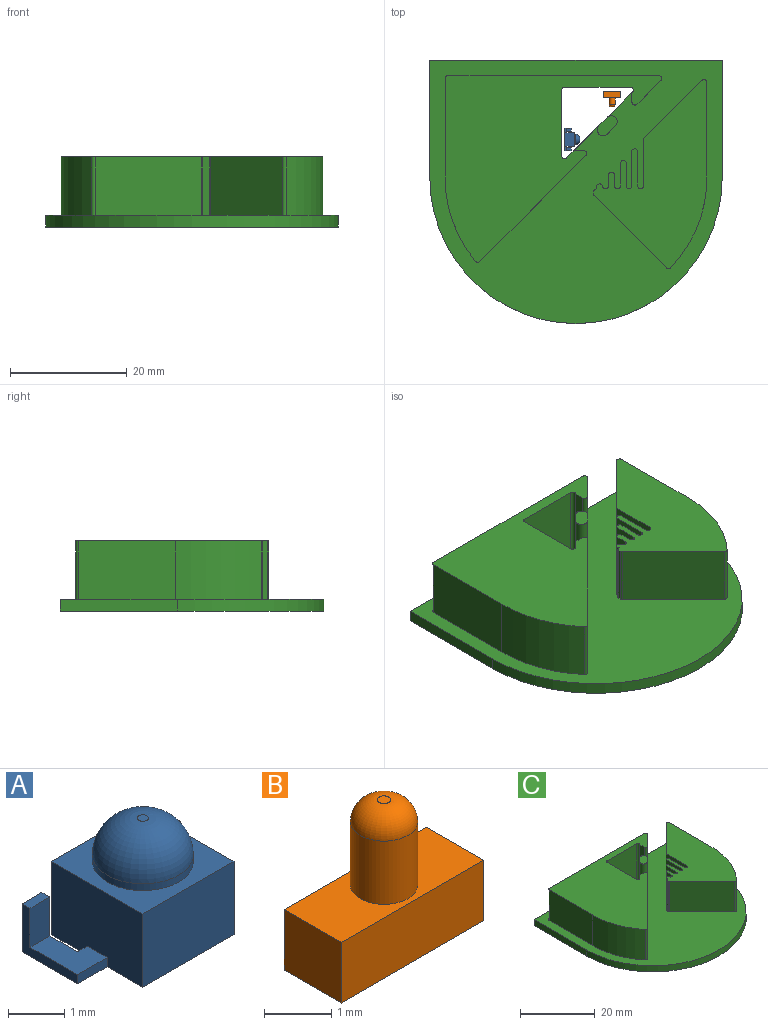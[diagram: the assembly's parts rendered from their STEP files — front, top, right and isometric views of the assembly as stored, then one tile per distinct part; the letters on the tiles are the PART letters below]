
ASSEMBLY  parts=3 mates=2
PART A: 25 faces, bbox 3.8x2.3x2.6 mm
  f0: plane 1.2x0.75mm, normal (0,0,1), area 0.7mm2, adj f3,f16,f17,f19,f20,f21
  f1: plane 2.3x1.6mm, normal (-1,0,0), area 3.6mm2, adj f2,f4,f5,f6,f10,f14,f15
  f2: plane 2.3x1.6mm, normal (0,-1,0), area 3.7mm2, adj f1,f3,f5,f6
  f3: plane 2.3x1.6mm, normal (1,0,0), area 3.6mm2, adj f0,f2,f4,f5,f6,f16,f20
  f4: plane 2.3x1.6mm, normal (0,1,0), area 3.7mm2, adj f1,f3,f5,f6
  f5: plane 2.3x2.3mm, normal (0,0,1), area 2.7mm2, adj f1,f2,f3,f4,f7
  f6: plane 3.8x2.3mm, normal (0,0,-1), area 6.9mm2, adj f1,f2,f3,f4,f10,f11,f12,f13
  f7: cylinder r=0.9mm len=1.8mm, axis (0,0,-1), area 0.8mm2, adj f5,f9
  f8: plane 0.2x0.2mm, normal (0,0,1), area 0mm2, adj f9
  f9: torus R=0.1mm, axis (0,0,1), area 4.8mm2, adj f7,f8
  f10: plane 0.75x0.2mm, normal (0,-1,0), area 0.2mm2, adj f1,f6,f11,f15
  f11: plane 1.4x1.05mm, normal (-1,0,0), area 0.5mm2, adj f6,f10,f12,f15,f23,f24
  f12: plane 1.05x0.5mm, normal (0,1,0), area 0.5mm2, adj f6,f11,f13,f24
  f13: plane 1.05x0.9mm, normal (1,0,0), area 0.3mm2, adj f6,f12,f14,f15,f23,f24
  f14: plane 0.25x0.2mm, normal (0,1,0), area 0.1mm2, adj f1,f6,f13,f15
  f15: plane 1.2x0.75mm, normal (0,0,1), area 0.7mm2, adj f1,f10,f11,f13,f14,f23
  f16: plane 0.25x0.2mm, normal (0,1,0), area 0.1mm2, adj f0,f3,f6,f17
  f17: plane 1.05x0.9mm, normal (-1,0,0), area 0.3mm2, adj f0,f6,f16,f18,f21,f22
  f18: plane 1.05x0.5mm, normal (0,1,0), area 0.5mm2, adj f6,f17,f19,f22
  f19: plane 1.4x1.05mm, normal (1,0,0), area 0.5mm2, adj f0,f6,f18,f20,f21,f22
  f20: plane 0.75x0.2mm, normal (0,-1,0), area 0.2mm2, adj f0,f3,f6,f19
  f21: plane 0.85x0.5mm, normal (0,-1,0), area 0.4mm2, adj f0,f17,f19,f22
  f22: plane 0.5x0.2mm, normal (0,0,1), area 0.1mm2, adj f17,f18,f19,f21
  f23: plane 0.85x0.5mm, normal (0,-1,0), area 0.4mm2, adj f11,f13,f15,f24
  f24: plane 0.5x0.2mm, normal (0,0,1), area 0.1mm2, adj f11,f12,f13,f23
PART B: 9 faces, bbox 3x1.2x2.7 mm
  f0: plane 3x1.1mm, normal (0,-1,0), area 3.3mm2, adj f1,f3,f4,f5
  f1: plane 1.2x1.1mm, normal (1,0,0), area 1.3mm2, adj f0,f2,f4,f5
  f2: plane 3x1.1mm, normal (0,1,0), area 3.3mm2, adj f1,f3,f4,f5
  f3: plane 1.2x1.1mm, normal (-1,0,0), area 1.3mm2, adj f0,f2,f4,f5
  f4: plane 3x1.2mm, normal (0,0,1), area 2.8mm2, adj f0,f1,f2,f3,f6
  f5: plane 3x1.2mm, normal (0,0,-1), area 3.6mm2, adj f0,f1,f2,f3
  f6: cylinder r=0.5mm len=1.15mm, axis (0,0,-1), area 3.6mm2, adj f4,f8
  f7: plane 0.2x0.2mm, normal (0,0,1), area 0mm2, adj f8
  f8: torus R=0.1mm, axis (0,0,1), area 1.4mm2, adj f6,f7
PART C: 65 faces, bbox 50x45x12 mm
  f0: plane 10x9.98mm, normal (-0.71,0.71,0), area 141.1mm2, adj f5,f6,f38,f63
  f1: plane 10x0.15mm, normal (-0.71,0.71,0), area 2.1mm2, adj f5,f6,f36,f48
  f2: plane 10x0.15mm, normal (-0.71,0.71,0), area 2.1mm2, adj f5,f6,f34,f47
  f3: plane 10x0.15mm, normal (-0.71,0.71,0), area 2.1mm2, adj f5,f6,f32,f46
  f4: plane 10x0.15mm, normal (-0.71,0.71,0), area 2.1mm2, adj f5,f6,f40,f45
  f5: plane 32.32x19.4mm, normal (0,0,1), area 320.3mm2, adj f0,f1,f2,f3,f4,f12,f13,f14
  f6: plane 50x45mm, normal (0,0,1), area 1008.8mm2, adj f0,f1,f2,f3,f4,f8,f9,f10
  f7: plane 50x45mm, normal (0,0,-1), area 1898.6mm2, adj f8,f9,f10,f11,f16,f17,f18,f53
  f8: cylinder r=25mm len=50mm, axis (0,0,-1), area 157.1mm2, adj f6,f7,f9,f11
  f9: plane 20x2mm, normal (1,0,0), area 40mm2, adj f6,f7,f8,f10
  f10: plane 50x2mm, normal (0,1,0), area 100mm2, adj f6,f7,f9,f11
  f11: plane 20x2mm, normal (-1,0,0), area 40mm2, adj f6,f7,f8,f10
  f12: plane 12.34x12.34mm, normal (-0.71,-0.71,0), area 174.5mm2, adj f5,f6,f61,f64
  f13: cylinder r=22.4mm len=15.88mm, axis (0,0,-1), area 174.8mm2, adj f5,f6,f14,f64
  f14: plane 15.79x10mm, normal (1,0,0), area 157.9mm2, adj f5,f6,f13,f63
  f15: plane 10x0.29mm, normal (-1,0,0), area 2.9mm2, adj f5,f6,f61,f62
  f16: plane 12x11.24mm, normal (-0.71,0.71,0), area 70.8mm2, adj f6,f7,f24,f26,f27,f28,f29,f30
  f17: plane 12x11.24mm, normal (1,0,0), area 134.9mm2, adj f7,f24,f53,f54
  f18: plane 12x11.24mm, normal (0,-1,0), area 134.9mm2, adj f7,f24,f54,f55
  f19: plane 10x4.05mm, normal (0.71,-0.71,0), area 57.3mm2, adj f6,f24,f56,f57
  f20: plane 36.02x10mm, normal (0,1,0), area 360.2mm2, adj f6,f24,f57,f58
  f21: plane 16.5x10mm, normal (-1,0,0), area 165mm2, adj f6,f22,f24,f58
  f22: cylinder r=22.4mm len=14.76mm, axis (0,0,-1), area 159.8mm2, adj f6,f21,f24,f59
  f23: plane 18.11x18.11mm, normal (0.71,-0.71,0), area 256.1mm2, adj f6,f24,f59,f60
  f24: plane 37.03x31.94mm, normal (0,0,1), area 562.3mm2, adj f16,f17,f18,f19,f20,f21,f22,f23
  f25: plane 10x1.41mm, normal (0.71,-0.71,0), area 20mm2, adj f6,f26,f29,f30
  f26: plane 3.41x3.41mm, normal (0,0,1), area 7.1mm2, adj f16,f25,f29,f30
  f27: plane 10x1.62mm, normal (-1,0,0), area 16.2mm2, adj f6,f16,f24,f56
  f28: plane 10x1.62mm, normal (0,1,0), area 16.2mm2, adj f6,f16,f24,f60
  f29: cylinder r=1mm len=10mm, axis (0,0,-1), area 31.4mm2, adj f6,f16,f25,f26
  f30: cylinder r=1mm len=10mm, axis (0,0,1), area 31.4mm2, adj f6,f16,f25,f26
  f31: plane 10x0.07mm, normal (1,0,0), area 0.7mm2, adj f5,f6,f44,f49
  f32: plane 10x2.07mm, normal (-1,0,0), area 20.7mm2, adj f3,f5,f6,f49
  f33: plane 10x2.07mm, normal (1,0,0), area 20.7mm2, adj f5,f6,f43,f50
  f34: plane 10x4.07mm, normal (-1,0,0), area 40.7mm2, adj f2,f5,f6,f50
  f35: plane 10x4.07mm, normal (1,0,0), area 40.7mm2, adj f5,f6,f42,f51
  f36: plane 10x6.07mm, normal (-1,0,0), area 60.7mm2, adj f1,f5,f6,f51
  f37: plane 10x6.07mm, normal (1,0,0), area 60.7mm2, adj f5,f6,f41,f52
  f38: plane 10x8.07mm, normal (-1,0,0), area 80.7mm2, adj f0,f5,f6,f52
  f39: plane 10x0.07mm, normal (0,1,0), area 0.7mm2, adj f5,f6,f40,f62
  f40: plane 10x0.57mm, normal (-1,0,0), area 5.7mm2, adj f4,f5,f6,f39
  f41: plane 10x0.15mm, normal (0.71,0.71,0), area 2.1mm2, adj f5,f6,f37,f48
  f42: plane 10x0.15mm, normal (0.71,0.71,0), area 2.1mm2, adj f5,f6,f35,f47
  f43: plane 10x0.15mm, normal (0.71,0.71,0), area 2.1mm2, adj f5,f6,f33,f46
  f44: plane 10x0.15mm, normal (0.71,0.71,0), area 2.1mm2, adj f5,f6,f31,f45
  f45: cylinder r=0.5mm len=10mm, axis (0,0,-1), area 7.9mm2, adj f4,f5,f6,f44
  f46: cylinder r=0.5mm len=10mm, axis (0,0,-1), area 7.9mm2, adj f3,f5,f6,f43
  f47: cylinder r=0.5mm len=10mm, axis (0,0,-1), area 7.9mm2, adj f2,f5,f6,f42
  f48: cylinder r=0.5mm len=10mm, axis (0,0,-1), area 7.9mm2, adj f1,f5,f6,f41
  f49: cylinder r=0.5mm len=10mm, axis (0,0,1), area 15.7mm2, adj f5,f6,f31,f32
  f50: cylinder r=0.5mm len=10mm, axis (0,0,1), area 15.7mm2, adj f5,f6,f33,f34
  f51: cylinder r=0.5mm len=10mm, axis (0,0,-1), area 15.7mm2, adj f5,f6,f35,f36
  f52: cylinder r=0.5mm len=10mm, axis (0,0,1), area 15.7mm2, adj f5,f6,f37,f38
  f53: cylinder r=0.5mm len=12mm, axis (0,0,1), area 14.1mm2, adj f7,f16,f17,f24
  f54: cylinder r=0.5mm len=12mm, axis (0,0,1), area 9.4mm2, adj f7,f17,f18,f24
  f55: cylinder r=0.5mm len=12mm, axis (0,0,1), area 14.1mm2, adj f7,f16,f18,f24
  f56: cylinder r=0.5mm len=10mm, axis (0,0,1), area 11.8mm2, adj f6,f19,f24,f27
  f57: cylinder r=0.5mm len=10mm, axis (0,0,-1), area 11.8mm2, adj f6,f19,f20,f24
  f58: cylinder r=0.5mm len=10mm, axis (0,0,1), area 7.9mm2, adj f6,f20,f21,f24
  f59: cylinder r=0.5mm len=10mm, axis (0,0,-1), area 8.3mm2, adj f6,f22,f23,f24
  f60: cylinder r=0.5mm len=10mm, axis (0,0,-1), area 11.8mm2, adj f6,f23,f24,f28
  f61: cylinder r=0.5mm len=10mm, axis (0,0,1), area 3.9mm2, adj f5,f6,f12,f15
  f62: cylinder r=0.5mm len=10mm, axis (0,0,1), area 7.9mm2, adj f5,f6,f15,f39
  f63: cylinder r=0.5mm len=10mm, axis (0,0,-1), area 11.8mm2, adj f0,f5,f6,f14
  f64: cylinder r=0.5mm len=10mm, axis (0,0,-1), area 8mm2, adj f5,f6,f12,f13
PLACE A rot(axis=(-0.58,0.58,-0.58),120deg) t=(-1.9,6.49,-1.33)mm
PLACE B rot(axis=(1,0,0),90deg) t=(6.18,14.71,-1.88)mm
PLACE C t=(0,0,-2.48)mm
MATE planar A.f4 <-> C.f7  axis (0,0,-1) through (-1.1,6.49,-2.48)mm
MATE planar B.f0 <-> C.f7  axis (0,0,-1) through (6.18,14.16,-2.48)mm
